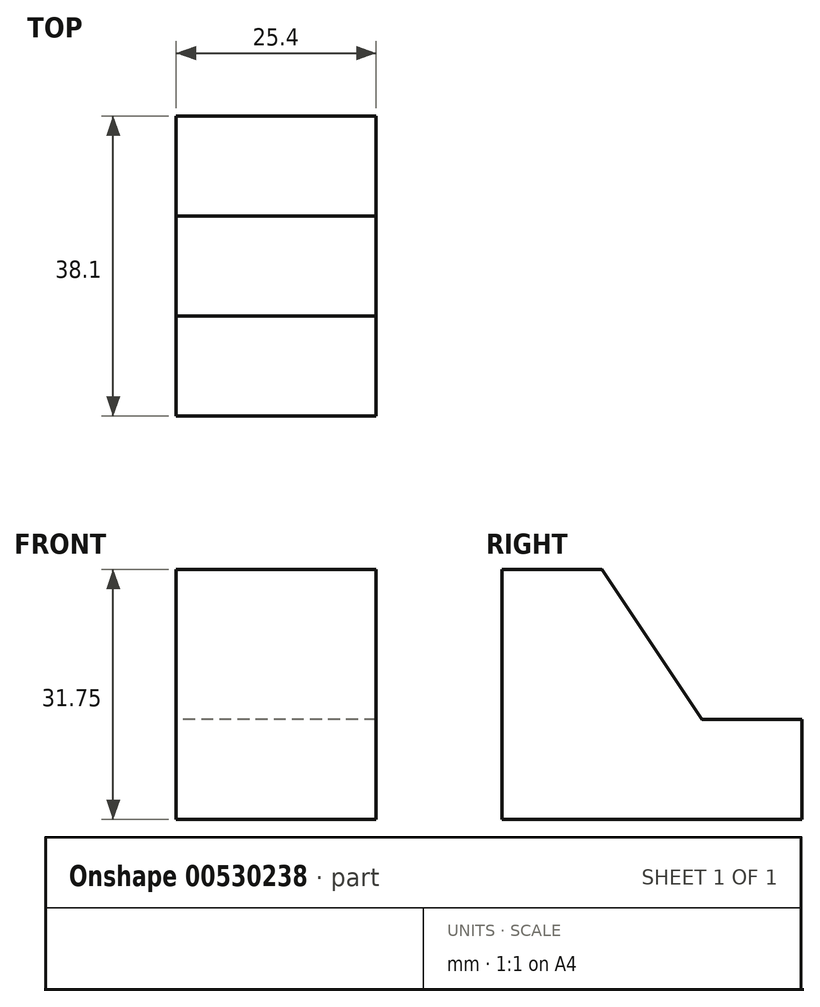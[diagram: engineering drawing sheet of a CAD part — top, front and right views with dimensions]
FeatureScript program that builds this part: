
annotation { "Feature Type Name" : "Feature", "Feature Type Description" : "" }
export const myFeature = defineFeature(function(context is Context, id is Id, definition is map)
    precondition{}
    {
        {
            var Q0;
            Q0=qCreatedBy(makeId("Right.planeOp"),FACE);
            var sketch = newSketch(context, id + "F0", { "sketchPlane" : qUnion([Q0])});
            skLineSegment(sketch, "E0", {"start": v(-69.03, 0) * mm, "end": v(-69.03, 31.75) * mm});
            skLineSegment(sketch, "E1", {"start": v(-69.03, 31.75) * mm, "end": v(-56.33, 31.75) * mm});
            skLineSegment(sketch, "E2", {"start": v(-56.33, 31.75) * mm, "end": v(-43.63, 12.7) * mm});
            skLineSegment(sketch, "E3", {"start": v(-43.63, 12.7) * mm, "end": v(-30.93, 12.7) * mm});
            skLineSegment(sketch, "E4", {"start": v(-30.93, 12.7) * mm, "end": v(-30.93, 0) * mm});
            skLineSegment(sketch, "E5", {"start": v(-30.93, 0) * mm, "end": v(-69.03, 0) * mm});
            skSolve(sketch);
        }
        {
            var Q0;
            Q0 = qSketchRegion(id + "F0", true);
            extrude(context, id + "F1", {"entities" : qUnion([Q0]), "depth" : 25.4 * mm, "offsetDistance" : 25.4 * mm});
        }
    });
